# Revit family: Storage-Multi_Level_Workstations-Teknion-BSMCHP_Mid_Height_Credenza_Open_Combo-R2018
name_source: partatom
category: Furniture
revit_build: Autodesk Revit 2018 (Build: 20170223_1515(x64)
units: mm (PartAtom-declared; Revit-internal decimal feet)

## family parameters
Always vertical = Yes
Cut with Voids When Loaded = No
OmniClass Number = 23.40.20.00
OmniClass Title = General Furniture and Specialties
Room Calculation Point = No
Shared = Yes
Work Plane-Based = No

## types (6) — shared parameters
Assembly Code = E2020200
Manufacturer = Teknion
Manufacturer Fax = 416.661.4586
Part Number = BSMCHP
Product Documentation Link = https://www.teknion.com
Product Line = Expansion Casegoods
Product Page URL = https://www.teknion.com
Series = Expansion Casegoods
Sustainability Data = https://www.teknion.com
URL = www.teknion.com
Unit Weight URL = http://www.teknion.com
Warranty = http://www.teknion.com

## per-type parameters (varying)
| type | Depth | Description | Height-Adjustable Worksurface Depth | Model | Top hole to Edge | Top hole to Top hole |
| 20" Depth, 35" Height-Adjustable Worksurface Depth | 20 " | Mid-Height Credenza for Height-Adjustable Peninsula - Open Combo, 20" Depth, 21" Height, 35" Height-Adjustable Worksurface Depth | 22.886 " | BSMCHP20_2135_ | 2.333 " | 22.886 " |
| 20" Depth, 46" Height-Adjustable Worksurface Depth | 20 " | Mid-Height Credenza for Height-Adjustable Peninsula - Open Combo, 20" Depth, 21" Height, 46" Height-Adjustable Worksurface Depth | 34.827 " | BSMCHP20_2146_ | 1.955 " | 34.827 " |
| 20" Depth, 52" Height-Adjustable Worksurface Depth | 20 " | Mid-Height Credenza for Height-Adjustable Peninsula - Open Combo, 20" Depth, 21" Height, 52" Height-Adjustable Worksurface Depth | 31.343 " | BSMCHP20_2152_ | 7.059 " | 31.343 " |
| 24" Depth, 35" Height-Adjustable Worksurface Depth | 24 " | Mid-Height Credenza for Height-Adjustable Peninsula - Open Combo, 24" Depth, 21" Height, 35" Height-Adjustable Worksurface Depth | 22.886 " | BSMCHP24_2135_ | 2.333 " | 22.886 " |
| 24" Depth, 46" Height-Adjustable Worksurface Depth | 24 " | Mid-Height Credenza for Height-Adjustable Peninsula - Open Combo, 24" Depth, 21" Height, 46" Height-Adjustable Worksurface Depth | 34.827 " | BSMCHP24_2146_ | 1.955 " | 34.827 " |
| 24" Depth, 52" Height-Adjustable Worksurface Depth | 24 " | Mid-Height Credenza for Height-Adjustable Peninsula - Open Combo, 24" Depth, 21" Height, 52" Height-Adjustable Worksurface Depth | 31.343 " | BSMCHP24_2152_ | 7.059 " | 31.343 " |

## geometry (parser evidence)
native form markers: Sweep x3
no freeform markers — native parametric forms only
